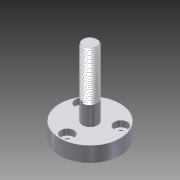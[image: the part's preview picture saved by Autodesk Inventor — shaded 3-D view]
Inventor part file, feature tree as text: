
AUTODESK INVENTOR PART (.ipt)
format: ipt  version: 2015 (Build 190159000, 159)  size: 571,392 bytes
history: native  units: in
note: dims shown in document units (in); Inventor stores cm internally (conversion verified against a paired STEP export)
features: chamfer x1, other x1, imported_body x1
ambient origin geometry x8: Origin, YZ Plane, XZ Plane, XY Plane, X Axis, Y Axis, Z Axis, Center Point
bodies: Body1 (feature_tree)
feature tree (3):
  chamfer  "Chamfer3"  [1 undecoded]
  other  "CapScrew.ipt1"
  imported_body  "Base1"
note: 1 required parameter value undecoded (feature->parameter linkage not recoverable at this tier; creation-order binding heuristic only, values carry confidence <= 0.55)
